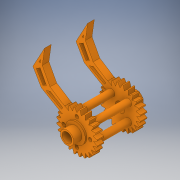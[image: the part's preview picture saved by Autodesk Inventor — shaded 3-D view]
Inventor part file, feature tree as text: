
AUTODESK INVENTOR PART (.ipt)
format: ipt  version: 2017 (Build 210142000, 142)  size: 649,216 bytes
history: native  units: in
note: dims shown in document units (in); Inventor stores cm internally (conversion verified against a paired STEP export)
features: extrude x30, sketch x30
ambient origin geometry x8: Origin, YZ Plane, XZ Plane, XY Plane, X Axis, Y Axis, Z Axis, Center Point
bodies: Solid1 (feature_tree)
feature tree (60):
  extrude  "Extrusion1"  Depth=0.5in
  extrude  "Extrusion2"  TaperAngle=150.0deg  [1 undecoded]
  extrude  "Extrusion3"  Depth=0.2in TaperAngle=0.0deg
  extrude  "Extrusion4"  TaperAngle=30.0deg  [1 undecoded]
  extrude  "Extrusion5"  TaperAngle=60.0deg  [1 undecoded]
  extrude  "Extrusion6"  Depth=0.2in TaperAngle=0.0deg
  extrude  "Extrusion7"  Depth=0.2in
  extrude  "Extrusion8"  Depth=0.2in TaperAngle=0.0deg
  extrude  "Extrusion9"  Depth=0.2in TaperAngle=0.0deg
  extrude  "Extrusion10"  Depth=0.4in
  extrude  "Extrusion11"  Depth=0.4in
  extrude  "Extrusion12"  Depth=0.4in
  extrude  "Extrusion13"  Depth=0.4in
  extrude  "Extrusion14"  Depth=0.2in TaperAngle=0.0deg
  extrude  "Extrusion15"  TaperAngle=60.0deg  [1 undecoded]
  extrude  "Extrusion16"  Depth=0.5in
  extrude  "Extrusion17"  Depth=0.2in TaperAngle=0.0deg
  extrude  "Extrusion18"  TaperAngle=135.0deg  [1 undecoded]
  extrude  "Extrusion19"  TaperAngle=45.0deg  [1 undecoded]
  extrude  "Extrusion20"  TaperAngle=135.0deg  [1 undecoded]
  extrude  "Extrusion21"  Depth=0.2in
  extrude  "Extrusion22"  Depth=1.1in TaperAngle=0.0deg
  extrude  "Extrusion23"  Depth=0.2in TaperAngle=0.0deg
  extrude  "Extrusion24"  Depth=0.2in TaperAngle=0.0deg
  extrude  "Extrusion25"  Depth=0.2in TaperAngle=0.0deg
  extrude  "Extrusion26"  Depth=0.2in TaperAngle=0.0deg
  extrude  "Extrusion27"  Depth=0.2in TaperAngle=0.0deg
  extrude  "Extrusion28"  Depth=0.2in TaperAngle=0.0deg
  extrude  "Extrusion29"  Depth=2.0in TaperAngle=0.0deg
  extrude  "Extrusion30"  Depth=0.05in TaperAngle=0.0deg
  sketch  "Sketch1"  dims[d0=0.5in d1=0.5in]
  sketch  "Sketch2"  dims[d2=15.0deg d3=150.0deg]
  sketch  "Sketch3"  dims[d4=30.0deg d5=0.2in d6=0.0in]
  sketch  "Sketch4"  dims[d7=0.5in d8=30.0deg]
  sketch  "Sketch5"  dims[d9=60.0deg d10=60.0deg]
  sketch  "Sketch6"  dims[d11=0.2in d12=0.0in d13=0.2in d14=0.0in]
  sketch  "Sketch7"  dims[d15=0.2in d16=0.0in d17=1.0in]
  sketch  "Sketch8"  dims[d18=0.2in d19=0.0in d20=0.2in d21=0.0in]
  sketch  "Sketch9"  dims[d22=0.3in d23=0.2in d24=0.0in]
  sketch  "Sketch10"  dims[d25=0.2in d26=0.0in d27=0.4in]
  sketch  "Sketch11"  dims[d28=0.11in d29=0.4in]
  sketch  "Sketch12"  dims[d30=0.11in d31=0.4in]
  sketch  "Sketch13"  dims[d32=0.4in d33=0.11in]
  sketch  "Sketch14"  dims[d34=0.11in d35=0.2in d36=0.0in]
  sketch  "Sketch15"  dims[d37=1.5in d38=60.0deg]
  sketch  "Sketch16"  dims[d39=30.0deg d40=0.5in]
  sketch  "Sketch17"  dims[d41=150.0deg d42=0.2in d43=0.0in]
  sketch  "Sketch18"  dims[d44=0.2in d45=0.0in d46=135.0deg]
  sketch  "Sketch19"  dims[d47=0.2in d48=45.0deg]
  sketch  "Sketch20"  dims[d49=45.0deg d50=135.0deg]
  sketch  "Sketch21"  dims[d51=0.2in d52=0.2in]
  sketch  "Sketch22"  dims[d53=0.2in d54=1.1in d55=0.0in]
  sketch  "Sketch23"  dims[d56=30.0deg d57=0.2in d58=0.0in]
  sketch  "Sketch24"  dims[d59=0.2in d60=0.0in d61=0.2in d62=0.0in]
  sketch  "Sketch25"  dims[d63=0.2in d64=0.0in d65=0.2in d66=0.0in]
  sketch  "Sketch26"  dims[d67=0.2in d68=0.0in d69=0.2in d70=0.0in]
  sketch  "Sketch27"  dims[d71=0.3in d72=0.2in d73=0.0in]
  sketch  "Sketch28"  dims[d74=0.2in d75=0.0in d76=2.0in d77=0.0in]
  sketch  "Sketch29"  dims[d78=2.0in d79=0.0in d80=2.0in d81=0.0in]
  sketch  "Sketch30"  dims[d82=0.6in d83=0.05in d84=0.0in d85=0.4in d86=0.25in d87=0.0in d88=0.3in d89=1.0in d90=0.0in d91=0.6in d92=0.05in d93=0.0in d94=0.4in d95=0.25in d96=0.0in d97=0.3in d98=1.0in d99=0.0in]
note: 7 required parameter values undecoded (feature->parameter linkage not recoverable at this tier; creation-order binding heuristic only, values carry confidence <= 0.55)
